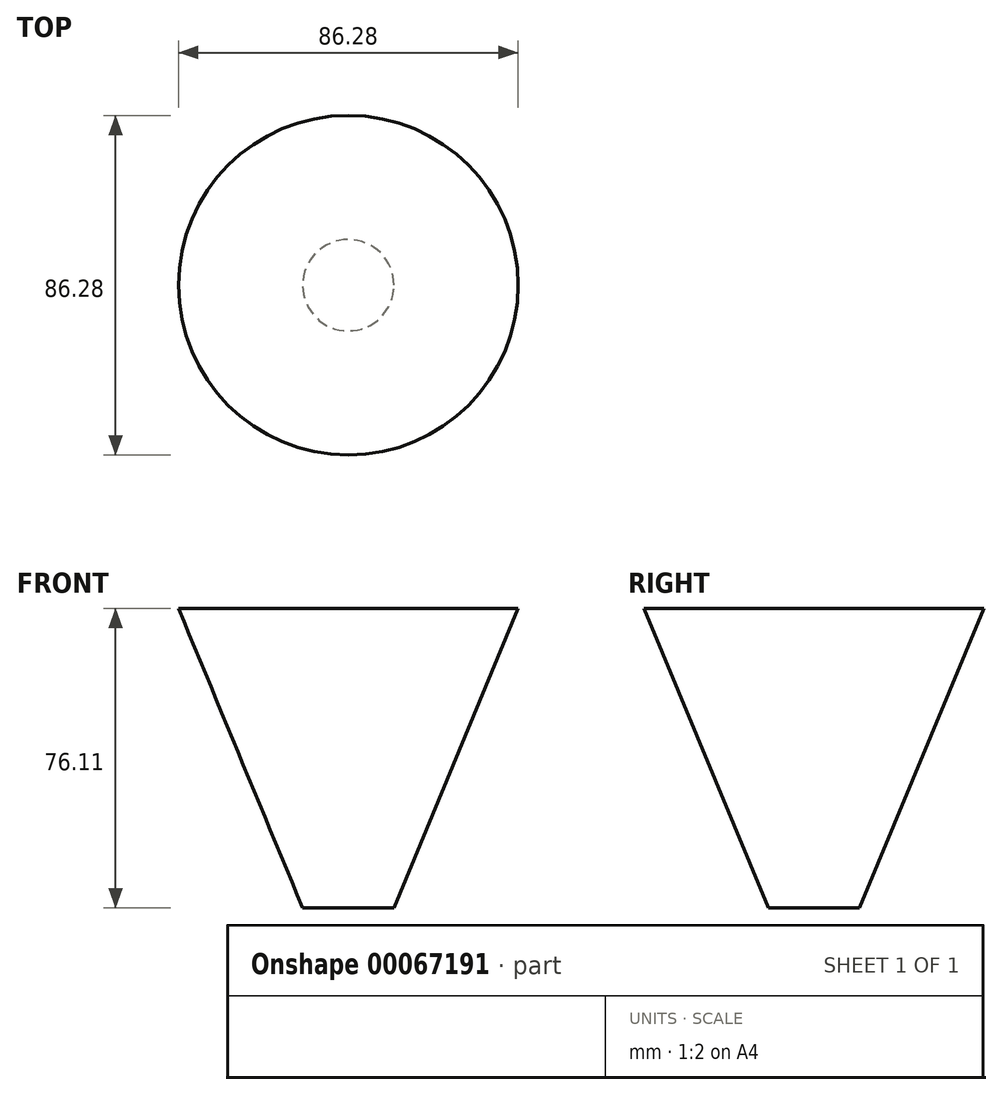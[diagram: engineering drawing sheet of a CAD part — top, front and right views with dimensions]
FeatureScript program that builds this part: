
annotation { "Feature Type Name" : "Feature", "Feature Type Description" : "" }
export const myFeature = defineFeature(function(context is Context, id is Id, definition is map)
    precondition{}
    {
        {
            var Q0;
            Q0=qCreatedBy(makeId("Front.planeOp"),FACE);
            var sketch = newSketch(context, id + "F0", { "sketchPlane" : qUnion([Q0])});
            skLineSegment(sketch, "E0", {"start": v(0, 0) * mm, "end": v(43.14, 0) * mm});
            skLineSegment(sketch, "E1", {"start": v(43.14, 0) * mm, "end": v(11.6, -76.1) * mm});
            skLineSegment(sketch, "E2", {"start": v(11.6, -76.1) * mm, "end": v(0, -76.1) * mm});
            skLineSegment(sketch, "E3", {"start": v(0, -76.1) * mm, "end": v(0, 0) * mm});
            skSolve(sketch);
        }
        {
            var Q0;
            Q0=makeQuery(id+"F0.imprint","IMPRINT",FACE,{"disambiguationData":[TD([[makeQuery(id+"F0.imprint","IMPRINT",EDGE,{"derivedFrom":sQuery(id+"F0.wireOp",EDGE,"E0")}),-1.0]])]});
            var Q1;
            Q1=sQuery(id+"F0.wireOp",EDGE,"E3");
            revolve(context, id + "F1", {"entities" : qUnion([Q0]), "axis" : qUnion([Q1]), "revolveType" : RevolveType.FULL});
        }
    });
